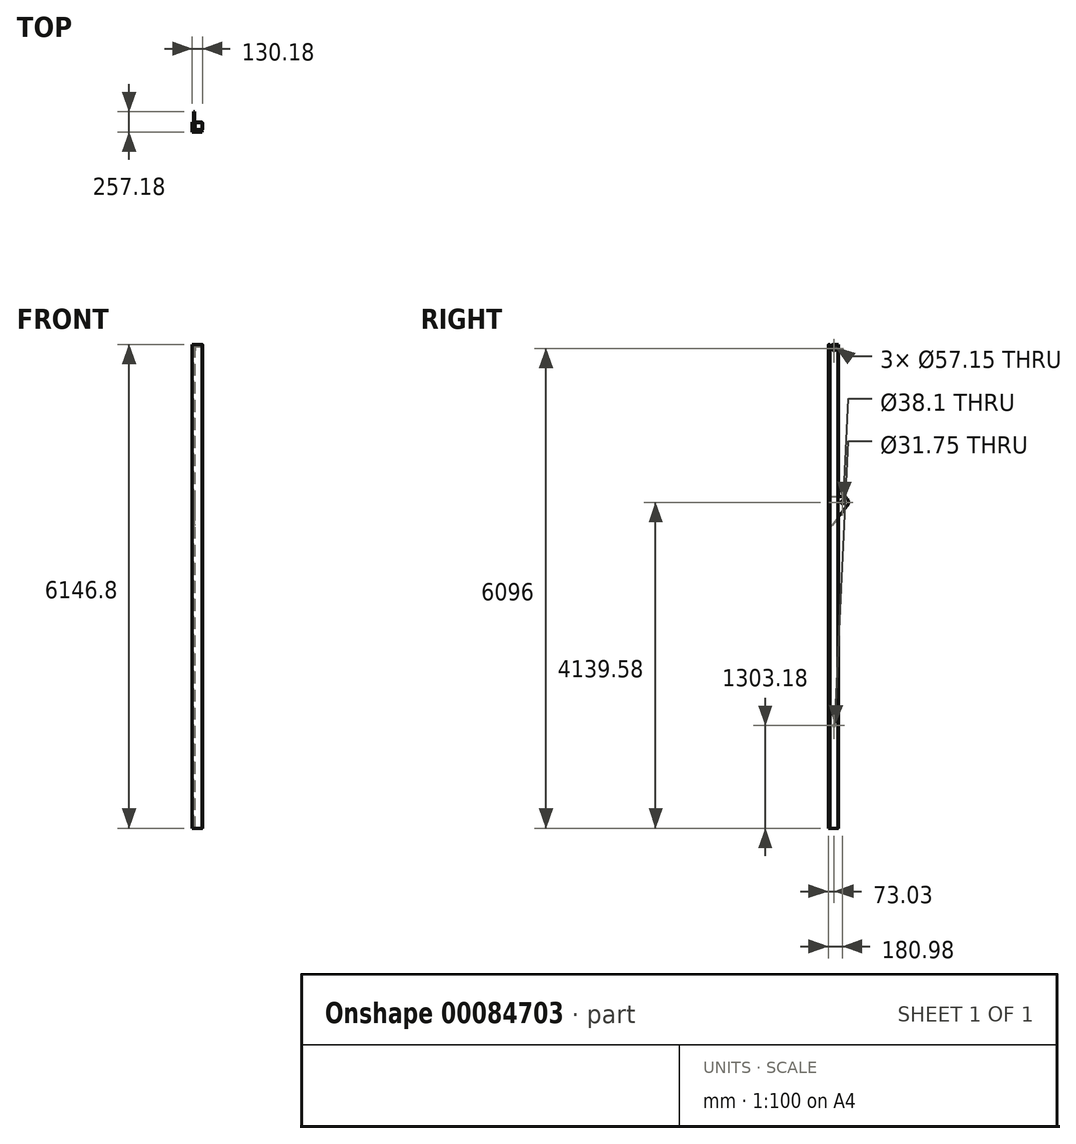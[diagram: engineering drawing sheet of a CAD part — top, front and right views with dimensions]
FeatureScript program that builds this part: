
annotation { "Feature Type Name" : "Feature", "Feature Type Description" : "" }
export const myFeature = defineFeature(function(context is Context, id is Id, definition is map)
    precondition{}
    {
        {
            var Q0;
            Q0=qCreatedBy(makeId("Right.planeOp"),FACE);
            var sketch = newSketch(context, id + "F0", { "sketchPlane" : qUnion([Q0])});
            skCircle(sketch, "E0", {"center": v(0, 0) * mm, "radius": 19.05 * mm});
            skCircle(sketch, "E1", {"center": v(0, 0) * mm, "radius": 28.58 * mm});
            skLineSegment(sketch, "E2", {"start": v(57.15, 50.8) * mm, "end": v(57.15, -6096) * mm});
            skCircle(sketch, "E3", {"center": v(107.95, -1956.42) * mm, "radius": 19.05 * mm});
            skCircle(sketch, "E4", {"center": v(107.95, -1956.42) * mm, "radius": 2838.45 * mm});
            skLineSegment(sketch, "E5", {"start": v(107.95, -1956.42) * mm, "end": v(0, -4792.82) * mm});
            skLineSegment(sketch, "E6", {"start": v(0, 0) * mm, "end": v(0, -4792.82) * mm});
            skCircle(sketch, "E7", {"center": v(107.95, -1956.42) * mm, "radius": 5276.85 * mm});
            skCircle(sketch, "E8", {"center": v(0, 0) * mm, "radius": 4792.82 * mm});
            skLineSegment(sketch, "E9", {"start": v(-4792.82, 0) * mm, "end": v(0, 0) * mm});
            skLineSegment(sketch, "E10", {"start": v(107.95, -1956.42) * mm, "end": v(-4792.82, 0) * mm});
            skCircle(sketch, "E11", {"center": v(0, -4792.82) * mm, "radius": 15.88 * mm});
            skSolve(sketch);
        }
        {
            var Q0;
            Q0=qCreatedBy(makeId("Top.planeOp"),FACE);
            var sketch = newSketch(context, id + "F12", { "sketchPlane" : qUnion([Q0])});
            skLineSegment(sketch, "E12.bottom", {"start": v(38.1, 50.8) * mm, "end": v(-38.1, 50.8) * mm});
            skLineSegment(sketch, "E12.top", {"start": v(38.1, -50.8) * mm, "end": v(-38.1, -50.8) * mm});
            skLineSegment(sketch, "E12.left", {"start": v(50.8, 38.1) * mm, "end": v(50.8, -38.1) * mm});
            skLineSegment(sketch, "E12.right", {"start": v(-50.8, 38.1) * mm, "end": v(-50.8, -38.1) * mm});
            skPoint(sketch, "E12.middle", {"position": v(0, 0) * mm});
            skPoint(sketch, "E13.visualSharp", {"position": v(-50.8, 50.8) * mm});
            skArc(sketch, "E13.filletArc", {"start": v(-38.1, 50.8) * mm, "mid": v(-47.08, 47.08) * mm, "end": v(-50.8, 38.1) * mm});
            skPoint(sketch, "E14.visualSharp", {"position": v(50.8, 50.8) * mm});
            skArc(sketch, "E14.filletArc", {"start": v(50.8, 38.1) * mm, "mid": v(47.08, 47.08) * mm, "end": v(38.1, 50.8) * mm});
            skPoint(sketch, "E15.visualSharp", {"position": v(50.8, -50.8) * mm});
            skArc(sketch, "E15.filletArc", {"start": v(38.1, -50.8) * mm, "mid": v(47.08, -47.08) * mm, "end": v(50.8, -38.1) * mm});
            skPoint(sketch, "E16.visualSharp", {"position": v(-50.8, -50.8) * mm});
            skArc(sketch, "E16.filletArc", {"start": v(-50.8, -38.1) * mm, "mid": v(-47.08, -47.08) * mm, "end": v(-38.1, -50.8) * mm});
            skArc(sketch, "E17.0", {"start": v(-38.1, 44.45) * mm, "mid": v(-42.6, 42.6) * mm, "end": v(-44.45, 38.1) * mm});
            skLineSegment(sketch, "E17.1", {"start": v(38.1, 44.45) * mm, "end": v(-38.1, 44.45) * mm});
            skLineSegment(sketch, "E17.2", {"start": v(-44.45, 38.1) * mm, "end": v(-44.45, -38.1) * mm});
            skArc(sketch, "E17.3", {"start": v(44.45, 38.1) * mm, "mid": v(42.6, 42.6) * mm, "end": v(38.1, 44.45) * mm});
            skArc(sketch, "E17.4", {"start": v(-44.45, -38.1) * mm, "mid": v(-42.6, -42.6) * mm, "end": v(-38.1, -44.45) * mm});
            skLineSegment(sketch, "E17.5", {"start": v(38.1, -44.45) * mm, "end": v(-38.1, -44.45) * mm});
            skArc(sketch, "E17.6", {"start": v(38.1, -44.45) * mm, "mid": v(42.6, -42.6) * mm, "end": v(44.45, -38.1) * mm});
            skLineSegment(sketch, "E17.7", {"start": v(44.45, 38.1) * mm, "end": v(44.45, -38.1) * mm});
            skLineSegment(sketch, "E18", {"start": v(-69.85, 44.45) * mm, "end": v(-69.85, -53.98) * mm});
            skLineSegment(sketch, "E19", {"start": v(-60.32, -63.5) * mm, "end": v(38.1, -63.5) * mm});
            skLineSegment(sketch, "E20", {"start": v(47.62, -73.02) * mm, "end": v(47.62, -73.02) * mm});
            skLineSegment(sketch, "E21", {"start": v(47.62, -73.02) * mm, "end": v(-79.38, -73.03) * mm});
            skLineSegment(sketch, "E22", {"start": v(-79.38, -73.03) * mm, "end": v(-79.38, 53.97) * mm});
            skLineSegment(sketch, "E23", {"start": v(-79.38, 53.97) * mm, "end": v(-79.38, 53.97) * mm});
            skPoint(sketch, "E24.visualSharp", {"position": v(-69.85, 53.97) * mm});
            skArc(sketch, "E24.filletArc", {"start": v(-69.85, 44.45) * mm, "mid": v(-72.64, 51.19) * mm, "end": v(-79.38, 53.97) * mm});
            skPoint(sketch, "E25.visualSharp", {"position": v(-69.85, -63.5) * mm});
            skArc(sketch, "E25.filletArc", {"start": v(-69.85, -53.98) * mm, "mid": v(-67.06, -60.71) * mm, "end": v(-60.32, -63.5) * mm});
            skPoint(sketch, "E26.visualSharp", {"position": v(47.62, -63.5) * mm});
            skArc(sketch, "E26.filletArc", {"start": v(47.63, -73.02) * mm, "mid": v(44.84, -66.29) * mm, "end": v(38.1, -63.5) * mm});
            skSolve(sketch);
        }
        {
            var Q0;
            Q0=makeQuery(id+"F12.imprint","IMPRINT",FACE,{"disambiguationData":[TD([[makeQuery(id+"F12.imprint","IMPRINT",EDGE,{"derivedFrom":sQuery(id+"F12.wireOp",EDGE,"E12.bottom")}),1.0]])]});
            extrude(context, id + "F1", {"entities" : qUnion([Q0]), "oppositeDirection" : true, "depth" : 6096 * mm, "hasSecondDirection" : true, "secondDirectionOppositeDirection" : false, "secondDirectionDepth" : 50.8 * mm});
        }
        {
            var Q0;
            Q0=makeQuery(id+"F12.imprint","IMPRINT",FACE,{"disambiguationData":[TD([[makeQuery(id+"F12.imprint","IMPRINT",EDGE,{"derivedFrom":sQuery(id+"F12.wireOp",EDGE,"E18")}),-1.0]])]});
            var Q1;
            Q1=makeQuery(id+"F1.opExtrude","CAP_FACE",FACE,{"disambiguationData":[OSD([sQuery(id+"F12.wireOp",EDGE,"E12.bottom"),sQuery(id+"F12.wireOp",EDGE,"E12.top"),sQuery(id+"F12.wireOp",EDGE,"E12.left"),sQuery(id+"F12.wireOp",EDGE,"E12.right"),sQuery(id+"F12.wireOp",EDGE,"E13.filletArc"),sQuery(id+"F12.wireOp",EDGE,"E14.filletArc"),sQuery(id+"F12.wireOp",EDGE,"E15.filletArc"),sQuery(id+"F12.wireOp",EDGE,"E16.filletArc"),sQuery(id+"F12.wireOp",EDGE,"E17.0"),sQuery(id+"F12.wireOp",EDGE,"E17.1"),sQuery(id+"F12.wireOp",EDGE,"E17.2"),sQuery(id+"F12.wireOp",EDGE,"E17.3"),sQuery(id+"F12.wireOp",EDGE,"E17.4"),sQuery(id+"F12.wireOp",EDGE,"E17.5"),sQuery(id+"F12.wireOp",EDGE,"E17.6"),sQuery(id+"F12.wireOp",EDGE,"E17.7")])],"isStart":true});
            var Q2;
            Q2=makeQuery(id+"F1.opExtrude","CAP_FACE",FACE,{"disambiguationData":[OSD([sQuery(id+"F12.wireOp",EDGE,"E12.bottom"),sQuery(id+"F12.wireOp",EDGE,"E12.top"),sQuery(id+"F12.wireOp",EDGE,"E12.left"),sQuery(id+"F12.wireOp",EDGE,"E12.right"),sQuery(id+"F12.wireOp",EDGE,"E13.filletArc"),sQuery(id+"F12.wireOp",EDGE,"E14.filletArc"),sQuery(id+"F12.wireOp",EDGE,"E15.filletArc"),sQuery(id+"F12.wireOp",EDGE,"E16.filletArc"),sQuery(id+"F12.wireOp",EDGE,"E17.0"),sQuery(id+"F12.wireOp",EDGE,"E17.1"),sQuery(id+"F12.wireOp",EDGE,"E17.2"),sQuery(id+"F12.wireOp",EDGE,"E17.3"),sQuery(id+"F12.wireOp",EDGE,"E17.4"),sQuery(id+"F12.wireOp",EDGE,"E17.5"),sQuery(id+"F12.wireOp",EDGE,"E17.6"),sQuery(id+"F12.wireOp",EDGE,"E17.7")])],"isStart":false});
            extrude(context, id + "F2", {"entities" : qUnion([Q0]), "endBound" : BoundingType.UP_TO_SURFACE, "endBoundEntityFace" : qUnion([Q1]), "depth" : 25.4 * mm, "hasSecondDirection" : true, "secondDirectionBound" : SecondDirectionBoundingType.UP_TO_SURFACE, "secondDirectionOppositeDirection" : true, "secondDirectionBoundEntityFace" : qUnion([Q2]), "secondDirectionDepth" : 25.4 * mm});
        }
        {
            var Q0;
            Q0=makeQuery(id+"F2.opExtrude","SWEPT_FACE",FACE,{"disambiguationData":[OSD([sQuery(id+"F12.wireOp",EDGE,"E18")])]});
            var sketch = newSketch(context, id + "F3", { "sketchPlane" : qUnion([Q0])});
            skCircle(sketch, "E27", {"center": v(0, -4792.82) * mm, "radius": 15.88 * mm});
            skCircle(sketch, "E28", {"center": v(0, 0) * mm, "radius": 19.05 * mm});
            skCircle(sketch, "E29", {"center": v(0, 0) * mm, "radius": 28.58 * mm});
            skSolve(sketch);
        }
        {
            var Q0;
            Q0=makeQuery(id+"F3.imprint","IMPRINT",FACE,{"disambiguationData":[TD([[makeQuery(id+"F3.imprint","IMPRINT",EDGE,{"derivedFrom":sQuery(id+"F3.wireOp",EDGE,"E27")}),1.0]])]});
            extrude(context, id + "F4", {"entities" : qUnion([Q0]), "operationType" : NewBodyOperationType.REMOVE, "endBound" : BoundingType.THROUGH_ALL, "oppositeDirection" : true, "depth" : 25.4 * mm});
        }
        {
            var Q0;
            Q0=makeQuery(id+"F3.imprint","IMPRINT",FACE,{"disambiguationData":[TD([[makeQuery(id+"F3.imprint","IMPRINT",EDGE,{"derivedFrom":sQuery(id+"F3.wireOp",EDGE,"E28")}),-1.0]])]});
            var Q1;
            Q1=makeQuery(id+"F3.imprint","IMPRINT",FACE,{"disambiguationData":[TD([[makeQuery(id+"F3.imprint","IMPRINT",EDGE,{"derivedFrom":sQuery(id+"F3.wireOp",EDGE,"E28")}),1.0]])]});
            extrude(context, id + "F5", {"entities" : qUnion([Q0, Q1]), "operationType" : NewBodyOperationType.REMOVE, "endBound" : BoundingType.THROUGH_ALL, "depth" : 25.4 * mm, "hasSecondDirection" : true, "secondDirectionBound" : SecondDirectionBoundingType.THROUGH_ALL, "secondDirectionOppositeDirection" : true, "secondDirectionDepth" : 25.4 * mm});
        }
        {
            var Q0;
            Q0=sQuery(id+"F0.wireOp",EDGE,"E3");
            extrude(context, id + "F6", {"bodyType" : ToolBodyType.SURFACE, "surfaceEntities" : qUnion([Q0]), "endBound" : BoundingType.SYMMETRIC, "depth" : 25.4 * mm});
        }
        {
            var Q0;
            Q0=makeQuery(id+"F1.opExtrude","SWEPT_FACE",FACE,{"disambiguationData":[OSD([sQuery(id+"F12.wireOp",EDGE,"E12.right")])]});
            var sketch = newSketch(context, id + "F7", { "sketchPlane" : qUnion([Q0])});
            skCircle(sketch, "E30", {"center": v(-107.95, -1956.42) * mm, "radius": 19.05 * mm});
            skLineSegment(sketch, "E31", {"start": v(38.1, -1880.22) * mm, "end": v(-107.95, -1880.22) * mm});
            skLineSegment(sketch, "E32", {"start": v(-167.48, -2004) * mm, "end": v(38.1, -2261.22) * mm});
            skLineSegment(sketch, "E33", {"start": v(38.1, -2261.22) * mm, "end": v(38.1, -1880.22) * mm});
            skArc(sketch, "E34", {"start": v(-107.95, -1880.22) * mm, "mid": v(-176.62, -1923.4) * mm, "end": v(-167.48, -2004) * mm});
            skSolve(sketch);
        }
        {
            var Q0;
            Q0=makeQuery(id+"F7.imprint","IMPRINT",FACE,{"disambiguationData":[TD([[makeQuery(id+"F7.imprint","IMPRINT",EDGE,{"derivedFrom":sQuery(id+"F7.wireOp",EDGE,"E30")}),-1.0]])]});
            var Q1;
            {var subQ0=sQuery(id+"F7.wireOp",EDGE,"E33");Q1=makeQuery(id+"F7.imprint","IMPRINT",FACE,{"disambiguationData":[TD([[makeQuery(id+"F7.imprint","IMPRINT",EDGE,{"derivedFrom":subQ0}),1.0]])]});}
            extrude(context, id + "F8", {"entities" : qUnion([Q0, Q1]), "depth" : 12.7 * mm});
        }
        {
            var Q0;
            Q0=makeQuery(id+"F8.opExtrude","SWEPT_EDGE",EDGE,{"disambiguationData":[OSD([sQuery(id+"F12.wireOp",EDGE,"E12.right"),sQuery(id+"F12.wireOp",EDGE,"E16.filletArc"),sQuery(id+"F7.wireOp",EDGE,"E31"),sQuery(id+"F7.wireOp",EDGE,"E33")])]});
            var Q1;
            Q1=makeQuery(id+"F8.opExtrude","SWEPT_EDGE",EDGE,{"disambiguationData":[OSD([sQuery(id+"F12.wireOp",EDGE,"E12.right"),sQuery(id+"F12.wireOp",EDGE,"E16.filletArc"),sQuery(id+"F7.wireOp",EDGE,"E32"),sQuery(id+"F7.wireOp",EDGE,"E33")])]});
            fillet(context, id + "F9", {"entities" : qUnion([Q0, Q1]), "radius" : 6.35 * mm, "tangentPropagation" : true, "allowEdgeOverflow" : false});
        }
        {
            var Q0;
            Q0=makeQuery(id+"F1.opExtrude","SWEPT_FACE",FACE,{"disambiguationData":[OSD([sQuery(id+"F12.wireOp",EDGE,"E12.left")])]});
            var sketch = newSketch(context, id + "F10", { "sketchPlane" : qUnion([Q0])});
            skArc(sketch, "E35", {"start": v(0, 50.8) * mm, "mid": v(-35.92, 35.92) * mm, "end": v(-50.8, 0) * mm});
            skLineSegment(sketch, "E36", {"start": v(-50.8, 0) * mm, "end": v(-50.8, 50.8) * mm});
            skLineSegment(sketch, "E37", {"start": v(-50.8, 50.8) * mm, "end": v(0, 50.8) * mm});
            skLineSegment(sketch, "E38", {"start": v(-50.8, 24.6) * mm, "end": v(-44.45, 24.6) * mm});
            skSolve(sketch);
        }
        {
            var Q0;
            {var subQ0=sQuery(id+"F10.wireOp",EDGE,"E37");var subQ1=sQuery(id+"F10.wireOp",EDGE,"E35");var subQ2=sQuery(id+"F12.wireOp",EDGE,"E12.left");var subQ3=makeQuery(id+"F10.imprint","INTERSECT",VERTEX,{"derivedFrom":[makeQuery(id+"F1.opExtrude","CAP_EDGE",EDGE,{"disambiguationData":[OSD([subQ2])],"isStart":true}),subQ1,subQ0]});Q0=makeQuery(id+"F10.imprint","IMPRINT",FACE,{"disambiguationData":[TD([[makeQuery(id+"F10.imprint","IMPRINT",EDGE,{"disambiguationData":[TD([[subQ3,-1.0]])],"derivedFrom":subQ1}),-1.0]])]});}
            var Q1;
            {var subQ0=sQuery(id+"F10.wireOp",EDGE,"E38");Q1=makeQuery(id+"F10.imprint","IMPRINT",FACE,{"disambiguationData":[TD([[makeQuery(id+"F10.imprint","IMPRINT",EDGE,{"derivedFrom":subQ0}),1.0]])]});}
            extrude(context, id + "F11", {"entities" : qUnion([Q0, Q1]), "operationType" : NewBodyOperationType.REMOVE, "endBound" : BoundingType.THROUGH_ALL, "oppositeDirection" : true, "depth" : 25.4 * mm});
        }
    });
